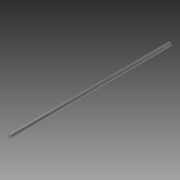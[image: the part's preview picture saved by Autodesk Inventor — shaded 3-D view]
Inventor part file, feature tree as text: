
AUTODESK INVENTOR PART (.ipt)
format: ipt  version: 2014 SP1 (Build 180222100, 222)  size: 91,136 bytes
history: native  units: in
note: dims shown in document units (in); Inventor stores cm internally (conversion verified against a paired STEP export)
features: extrude x1, sketch x1
ambient origin geometry x8: Origin, YZ Plane, XZ Plane, XY Plane, X Axis, Y Axis, Z Axis, Center Point
bodies: Solid1 (feature_tree)
feature tree (2):
  extrude  "Extrusion1"  Depth=25.0in TaperAngle=0.0deg
  sketch  "Sketch1"  dims[d0=0.5in d1=25.0in d2=0.0in]
